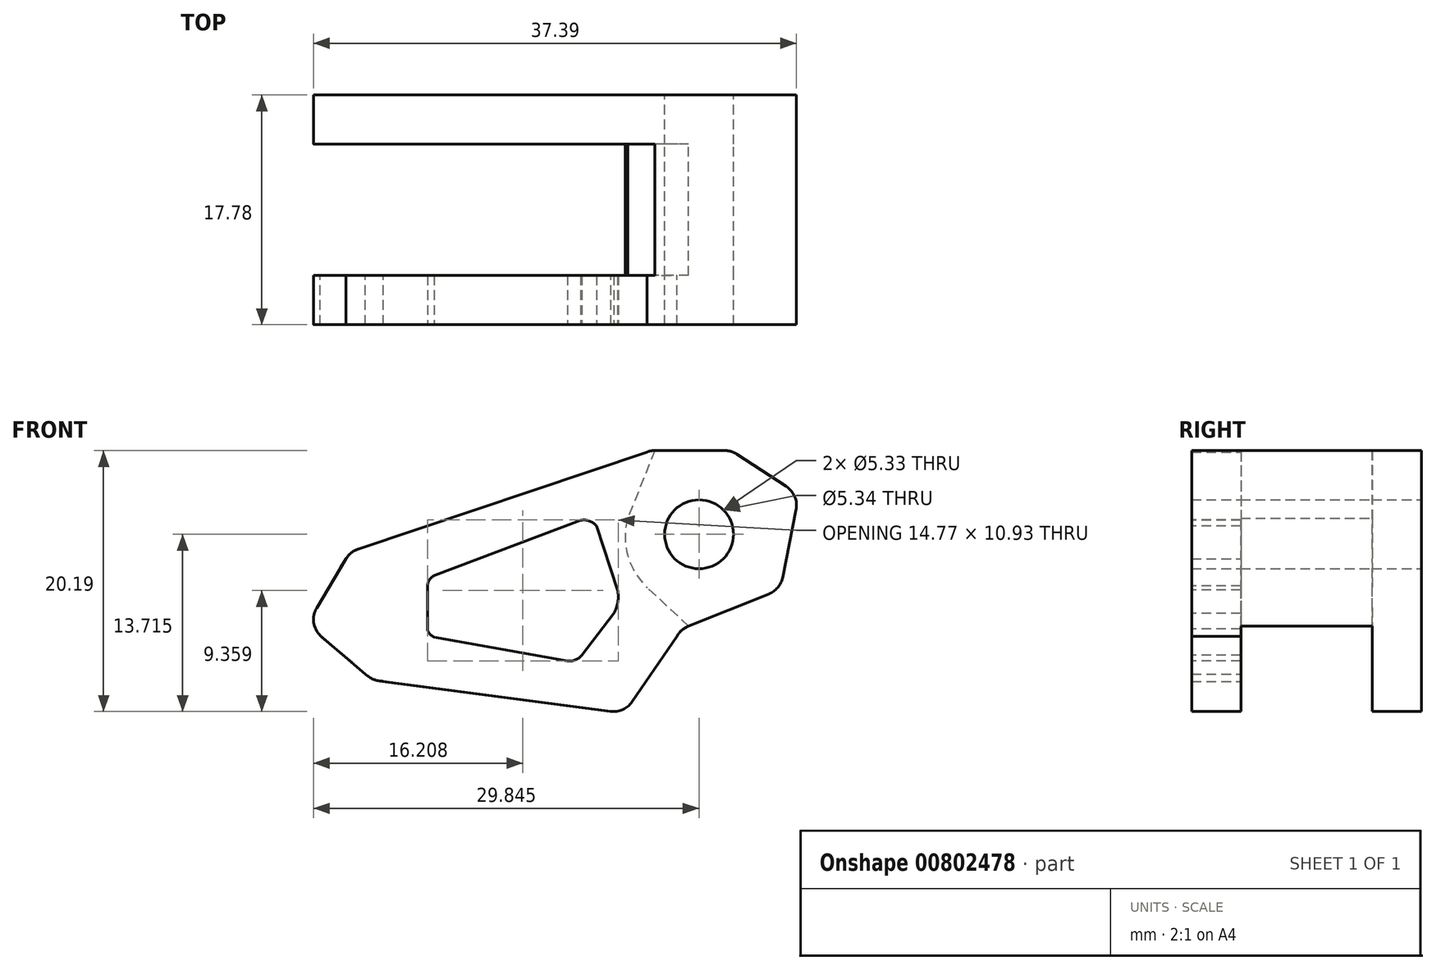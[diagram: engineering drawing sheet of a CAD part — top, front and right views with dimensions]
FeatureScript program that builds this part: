
annotation { "Feature Type Name" : "Feature", "Feature Type Description" : "" }
export const myFeature = defineFeature(function(context is Context, id is Id, definition is map)
    precondition{}
    {
        {
            var Q0;
            Q0=qCreatedBy(makeId("Front.planeOp"),FACE);
            var sketch = newSketch(context, id + "F0", { "sketchPlane" : qUnion([Q0])});
            skLineSegment(sketch, "E0.bottom", {"start": v(17.62, 20.63) * mm, "end": v(23.83, 20.63) * mm});
            skCircle(sketch, "E1", {"center": v(21.33, 14.16) * mm, "radius": 2.67 * mm});
            skLineSegment(sketch, "E2", {"start": v(27.62, 9.89) * mm, "end": v(20.02, 6.85) * mm});
            skLineSegment(sketch, "E3", {"start": v(20.02, 6.85) * mm, "end": v(15.55, 0.31) * mm});
            skLineSegment(sketch, "E4", {"start": v(15.55, 0.31) * mm, "end": v(-3.92, 2.87) * mm});
            skLineSegment(sketch, "E5", {"start": v(-3.92, 2.87) * mm, "end": v(-9.02, 7.18) * mm});
            skLineSegment(sketch, "E6", {"start": v(-9.02, 7.18) * mm, "end": v(-5.66, 12.81) * mm});
            skLineSegment(sketch, "E7", {"start": v(-5.66, 12.81) * mm, "end": v(17.62, 20.63) * mm});
            skLineSegment(sketch, "E8", {"start": v(23.83, 20.63) * mm, "end": v(29.08, 17.2) * mm});
            skLineSegment(sketch, "E9", {"start": v(29.08, 17.2) * mm, "end": v(27.62, 9.89) * mm});
            skPoint(sketch, "E10.trimOffspring.start.orphan", {"position": v(29.08, 10.47) * mm});
            skPoint(sketch, "E11.orphan", {"position": v(29.08, 0.31) * mm});
            skPoint(sketch, "E0.right.start.orphan", {"position": v(29.08, 20.63) * mm});
            skSolve(sketch);
        }
        {
            var Q0;
            Q0 = qSketchRegion(id + "F0", true);
            extrude(context, id + "F1", {"entities" : qUnion([Q0]), "depth" : 3.8 * mm, "offsetDistance" : 25.4 * mm});
        }
        {
            var Q0;
            Q0=makeQuery(id+"F1.opExtrude","SWEPT_EDGE",EDGE,{"disambiguationData":[OSD([sQuery(id+"F0.wireOp",EDGE,"E4"),sQuery(id+"F0.wireOp",EDGE,"E5")])]});
            var Q1;
            Q1=makeQuery(id+"F1.opExtrude","SWEPT_EDGE",EDGE,{"disambiguationData":[OSD([sQuery(id+"F0.wireOp",EDGE,"E3"),sQuery(id+"F0.wireOp",EDGE,"E4")])]});
            var Q2;
            Q2=makeQuery(id+"F1.opExtrude","SWEPT_EDGE",EDGE,{"disambiguationData":[OSD([sQuery(id+"F0.wireOp",EDGE,"E2"),sQuery(id+"F0.wireOp",EDGE,"E3")])]});
            var Q3;
            Q3=makeQuery(id+"F1.opExtrude","SWEPT_EDGE",EDGE,{"disambiguationData":[OSD([sQuery(id+"F0.wireOp",EDGE,"E2"),sQuery(id+"F0.wireOp",EDGE,"E9")])]});
            var Q4;
            Q4=makeQuery(id+"F1.opExtrude","SWEPT_EDGE",EDGE,{"disambiguationData":[OSD([sQuery(id+"F0.wireOp",EDGE,"E0.bottom"),sQuery(id+"F0.wireOp",EDGE,"E8")])]});
            var Q5;
            Q5=makeQuery(id+"F1.opExtrude","SWEPT_EDGE",EDGE,{"disambiguationData":[OSD([sQuery(id+"F0.wireOp",EDGE,"E7"),sQuery(id+"F0.wireOp",EDGE,"E0.bottom")])]});
            var Q6;
            Q6=makeQuery(id+"F1.opExtrude","SWEPT_EDGE",EDGE,{"disambiguationData":[OSD([sQuery(id+"F0.wireOp",EDGE,"E8"),sQuery(id+"F0.wireOp",EDGE,"E9")])]});
            var Q7;
            Q7=makeQuery(id+"F1.opExtrude","SWEPT_EDGE",EDGE,{"disambiguationData":[OSD([sQuery(id+"F0.wireOp",EDGE,"E6"),sQuery(id+"F0.wireOp",EDGE,"E7")])]});
            var Q8;
            Q8=makeQuery(id+"F1.opExtrude","SWEPT_EDGE",EDGE,{"disambiguationData":[OSD([sQuery(id+"F0.wireOp",EDGE,"E5"),sQuery(id+"F0.wireOp",EDGE,"E6")])]});
            fillet(context, id + "F2", {"entities" : qUnion([Q0, Q1, Q2, Q3, Q4, Q5, Q6, Q7, Q8]), "radius" : 1.78 * mm, "tangentPropagation" : true, "allowEdgeOverflow" : false});
        }
        {
            var Q0;
            Q0=makeQuery(id+"F1.opExtrude","CAP_FACE",FACE,{"disambiguationData":[OSD([sQuery(id+"F0.wireOp",EDGE,"E1"),sQuery(id+"F0.wireOp",EDGE,"E2"),sQuery(id+"F0.wireOp",EDGE,"E3"),sQuery(id+"F0.wireOp",EDGE,"E4"),sQuery(id+"F0.wireOp",EDGE,"E5"),sQuery(id+"F0.wireOp",EDGE,"E6"),sQuery(id+"F0.wireOp",EDGE,"E7"),sQuery(id+"F0.wireOp",EDGE,"E0.bottom"),sQuery(id+"F0.wireOp",EDGE,"E8"),sQuery(id+"F0.wireOp",EDGE,"E9")])],"isStart":false});
            var sketch = newSketch(context, id + "F3", { "sketchPlane" : qUnion([Q0])});
            skCircle(sketch, "E12", {"center": v(21.33, 14.16) * mm, "radius": 2.67 * mm});
            skLineSegment(sketch, "E13", {"start": v(17.9, 20.63) * mm, "end": v(15.82, 15.4) * mm});
            skLineSegment(sketch, "E14", {"start": v(20.52, 7.05) * mm, "end": v(17.33, 10.03) * mm});
            skArc(sketch, "E15", {"start": v(15.82, 15.4) * mm, "mid": v(15.82, 12.5) * mm, "end": v(17.33, 10.03) * mm});
            skLineSegment(sketch, "E16", {"start": v(17.9, 20.63) * mm, "end": v(23.3, 20.63) * mm});
            skLineSegment(sketch, "E17", {"start": v(24.27, 20.34) * mm, "end": v(28.07, 17.86) * mm});
            skLineSegment(sketch, "E18", {"start": v(28.85, 16.02) * mm, "end": v(27.8, 10.83) * mm});
            skLineSegment(sketch, "E19", {"start": v(20.52, 7.05) * mm, "end": v(26.72, 9.53) * mm});
            skArc(sketch, "E20", {"start": v(24.27, 20.34) * mm, "mid": v(23.8, 20.56) * mm, "end": v(23.3, 20.63) * mm});
            skArc(sketch, "E21", {"start": v(28.85, 16.02) * mm, "mid": v(28.74, 17.06) * mm, "end": v(28.07, 17.86) * mm});
            skArc(sketch, "E22", {"start": v(26.72, 9.53) * mm, "mid": v(27.43, 10.04) * mm, "end": v(27.8, 10.83) * mm});
            skSolve(sketch);
        }
        {
            var Q0;
            Q0 = qSketchRegion(id + "F3", true);
            extrude(context, id + "F4", {"entities" : qUnion([Q0]), "operationType" : NewBodyOperationType.ADD, "depth" : 10.16 * mm, "offsetDistance" : 25.4 * mm});
        }
        {
            var Q0;
            Q0=makeQuery(id+"F4.opExtrude","CAP_FACE",FACE,{"disambiguationData":[OSD([sQuery(id+"F3.wireOp",EDGE,"E12"),sQuery(id+"F3.wireOp",EDGE,"E13"),sQuery(id+"F3.wireOp",EDGE,"E14"),sQuery(id+"F3.wireOp",EDGE,"E15"),sQuery(id+"F3.wireOp",EDGE,"E16"),sQuery(id+"F3.wireOp",EDGE,"E17"),sQuery(id+"F3.wireOp",EDGE,"E18"),sQuery(id+"F3.wireOp",EDGE,"E19"),sQuery(id+"F3.wireOp",EDGE,"E20"),sQuery(id+"F3.wireOp",EDGE,"E21"),sQuery(id+"F3.wireOp",EDGE,"E22")])],"isStart":false});
            var sketch = newSketch(context, id + "F5", { "sketchPlane" : qUnion([Q0])});
            skLineSegment(sketch, "E23", {"start": v(20.52, 7.05) * mm, "end": v(26.72, 9.53) * mm});
            skLineSegment(sketch, "E24", {"start": v(27.8, 10.83) * mm, "end": v(28.85, 16.02) * mm});
            skLineSegment(sketch, "E25", {"start": v(28.07, 17.86) * mm, "end": v(24.27, 20.34) * mm});
            skLineSegment(sketch, "E26", {"start": v(23.3, 20.63) * mm, "end": v(17.9, 20.63) * mm});
            skLineSegment(sketch, "E27", {"start": v(17.3, 20.52) * mm, "end": v(-5.02, 13.03) * mm});
            skLineSegment(sketch, "E28", {"start": v(-6, 12.26) * mm, "end": v(-8.26, 8.46) * mm});
            skLineSegment(sketch, "E29", {"start": v(-7.98, 6.33) * mm, "end": v(-4.5, 3.35) * mm});
            skLineSegment(sketch, "E30", {"start": v(-3.12, 2.77) * mm, "end": v(14.5, 0.45) * mm});
            skLineSegment(sketch, "E31", {"start": v(16.13, 1.16) * mm, "end": v(19.62, 6.26) * mm});
            skArc(sketch, "E32", {"start": v(17.9, 20.63) * mm, "mid": v(17.6, 20.6) * mm, "end": v(17.3, 20.52) * mm});
            skArc(sketch, "E33", {"start": v(24.27, 20.34) * mm, "mid": v(23.8, 20.56) * mm, "end": v(23.3, 20.63) * mm});
            skArc(sketch, "E34", {"start": v(28.85, 16.02) * mm, "mid": v(28.74, 17.06) * mm, "end": v(28.07, 17.86) * mm});
            skArc(sketch, "E35", {"start": v(26.72, 9.53) * mm, "mid": v(27.43, 10.04) * mm, "end": v(27.8, 10.83) * mm});
            skArc(sketch, "E36", {"start": v(20.52, 7.05) * mm, "mid": v(20, 6.73) * mm, "end": v(19.62, 6.26) * mm});
            skArc(sketch, "E37", {"start": v(14.5, 0.45) * mm, "mid": v(15.42, 0.58) * mm, "end": v(16.13, 1.16) * mm});
            skArc(sketch, "E38", {"start": v(-4.5, 3.35) * mm, "mid": v(-3.86, 2.93) * mm, "end": v(-3.12, 2.77) * mm});
            skArc(sketch, "E39", {"start": v(-8.26, 8.46) * mm, "mid": v(-8.5, 7.35) * mm, "end": v(-7.98, 6.33) * mm});
            skArc(sketch, "E40", {"start": v(-5.02, 13.03) * mm, "mid": v(-5.57, 12.73) * mm, "end": v(-6, 12.26) * mm});
            skCircle(sketch, "E41", {"center": v(21.33, 14.16) * mm, "radius": 2.67 * mm});
            skSolve(sketch);
        }
        {
            var Q0;
            Q0 = qSketchRegion(id + "F5", true);
            extrude(context, id + "F6", {"entities" : qUnion([Q0]), "operationType" : NewBodyOperationType.ADD, "depth" : 3.8 * mm, "offsetDistance" : 25.4 * mm});
        }
        {
            var Q0;
            Q0=makeQuery(id+"F6.opExtrude","CAP_FACE",FACE,{"disambiguationData":[OSD([sQuery(id+"F5.wireOp",EDGE,"E23"),sQuery(id+"F5.wireOp",EDGE,"E24"),sQuery(id+"F5.wireOp",EDGE,"E25"),sQuery(id+"F5.wireOp",EDGE,"E26"),sQuery(id+"F5.wireOp",EDGE,"E27"),sQuery(id+"F5.wireOp",EDGE,"E28"),sQuery(id+"F5.wireOp",EDGE,"E29"),sQuery(id+"F5.wireOp",EDGE,"E30"),sQuery(id+"F5.wireOp",EDGE,"E31"),sQuery(id+"F5.wireOp",EDGE,"E32"),sQuery(id+"F5.wireOp",EDGE,"E33"),sQuery(id+"F5.wireOp",EDGE,"E34"),sQuery(id+"F5.wireOp",EDGE,"E35"),sQuery(id+"F5.wireOp",EDGE,"E36"),sQuery(id+"F5.wireOp",EDGE,"E37"),sQuery(id+"F5.wireOp",EDGE,"E38"),sQuery(id+"F5.wireOp",EDGE,"E39"),sQuery(id+"F5.wireOp",EDGE,"E40"),sQuery(id+"F5.wireOp",EDGE,"E41")])],"isStart":false});
            var sketch = newSketch(context, id + "F7", { "sketchPlane" : qUnion([Q0])});
            skLineSegment(sketch, "E42", {"start": v(12.17, 15.24) * mm, "end": v(0.9, 10.97) * mm});
            skLineSegment(sketch, "E43", {"start": v(0.31, 10.75) * mm, "end": v(0.31, 6.83) * mm});
            skLineSegment(sketch, "E44", {"start": v(0.31, 6.3) * mm, "end": v(11.82, 4.22) * mm});
            skLineSegment(sketch, "E45", {"start": v(12.26, 4.8) * mm, "end": v(14.73, 8.02) * mm});
            skLineSegment(sketch, "E46", {"start": v(15.37, 8.85) * mm, "end": v(13.12, 15.6) * mm});
            skArc(sketch, "E47", {"start": v(13.39, 14.78) * mm, "mid": v(12.85, 15.19) * mm, "end": v(12.17, 15.24) * mm});
            skArc(sketch, "E48", {"start": v(14.73, 8.02) * mm, "mid": v(15.05, 8.9) * mm, "end": v(15.03, 9.85) * mm});
            skArc(sketch, "E49", {"start": v(11.15, 4.34) * mm, "mid": v(11.76, 4.43) * mm, "end": v(12.26, 4.8) * mm});
            skArc(sketch, "E50", {"start": v(0.9, 10.97) * mm, "mid": v(0.48, 10.65) * mm, "end": v(0.31, 10.16) * mm});
            skArc(sketch, "E51", {"start": v(0.31, 6.83) * mm, "mid": v(0.48, 6.45) * mm, "end": v(0.82, 6.2) * mm});
            skSolve(sketch);
        }
        {
            var Q0;
            Q0 = qSketchRegion(id + "F7", true);
            extrude(context, id + "F8", {"entities" : qUnion([Q0]), "operationType" : NewBodyOperationType.REMOVE, "oppositeDirection" : true, "depth" : 5.08 * mm, "offsetDistance" : 25.4 * mm});
        }
    });
